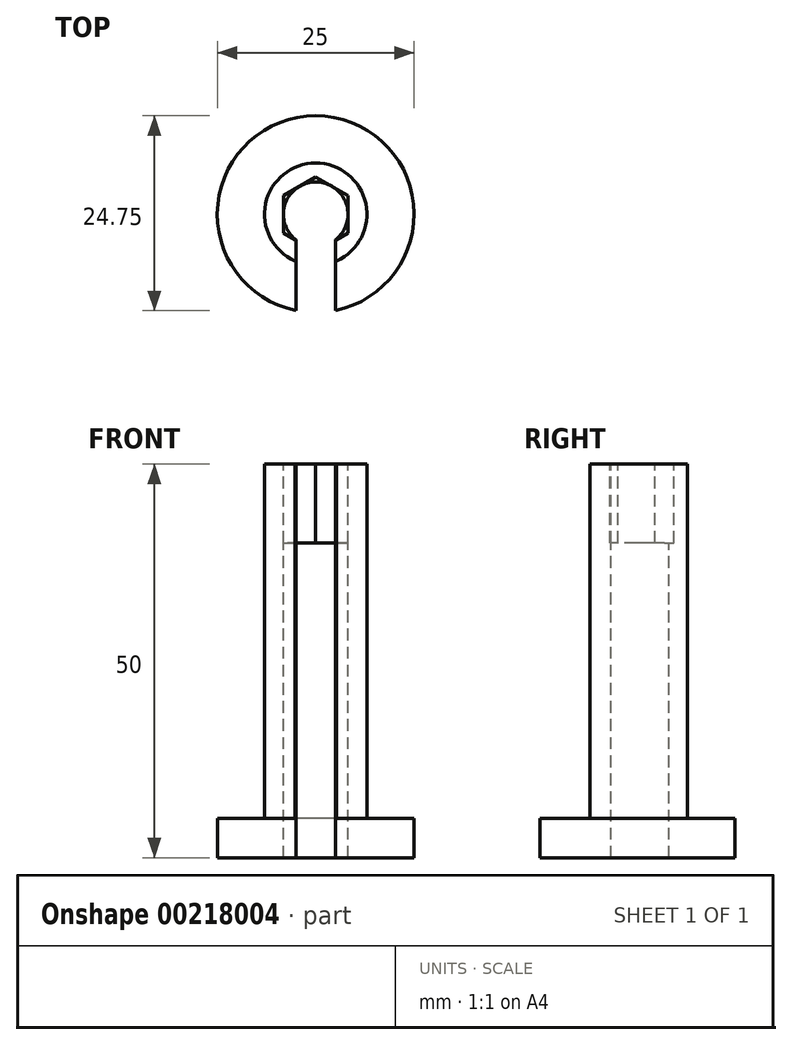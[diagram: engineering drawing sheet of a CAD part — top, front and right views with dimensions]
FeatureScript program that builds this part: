
annotation { "Feature Type Name" : "Feature", "Feature Type Description" : "" }
export const myFeature = defineFeature(function(context is Context, id is Id, definition is map)
    precondition{}
    {
        {
            var Q0;
            Q0=qCreatedBy(makeId("Top.planeOp"),FACE);
            var sketch = newSketch(context, id + "F0", { "sketchPlane" : qUnion([Q0])});
            skCircle(sketch, "E0", {"center": v(0, 0) * mm, "radius": 12.5 * mm});
            skCircle(sketch, "E1", {"center": v(0, 0) * mm, "radius": 6.5 * mm});
            skSolve(sketch);
        }
        {
            var Q0;
            Q0=makeQuery(id+"F0.imprint","IMPRINT",FACE,{"disambiguationData":[TD([[makeQuery(id+"F0.imprint","IMPRINT",EDGE,{"derivedFrom":sQuery(id+"F0.wireOp",EDGE,"E1")}),1.0]])]});
            extrude(context, id + "F1", {"entities" : qUnion([Q0]), "depth" : 50 * mm});
        }
        {
            var Q0;
            Q0 = qSketchRegion(id + "F0", true);
            var Q1;
            Q1 = qSketchRegion(id + "F5", true);
            extrude(context, id + "F2", {"entities" : qUnion([Q0, Q1]), "operationType" : NewBodyOperationType.ADD, "depth" : 5 * mm});
        }
        {
            var Q0;
            Q0=makeQuery(id+"F1.opExtrude","CAP_FACE",FACE,{"disambiguationData":[OSD([sQuery(id+"F0.wireOp",EDGE,"E1")])],"isStart":false});
            var sketch = newSketch(context, id + "F3", { "sketchPlane" : qUnion([Q0])});
            skLineSegment(sketch, "E2", {"start": v(0, 4.73) * mm, "end": v(-4.1, 2.37) * mm});
            skLineSegment(sketch, "E3", {"start": v(-4.1, 2.37) * mm, "end": v(-4.1, -2.37) * mm});
            skLineSegment(sketch, "E4", {"start": v(-4.1, -2.37) * mm, "end": v(0, -4.73) * mm});
            skLineSegment(sketch, "E5", {"start": v(0, -4.73) * mm, "end": v(4.1, -2.37) * mm});
            skLineSegment(sketch, "E6", {"start": v(4.1, -2.37) * mm, "end": v(4.1, 2.37) * mm});
            skLineSegment(sketch, "E7", {"start": v(4.1, 2.37) * mm, "end": v(0, 4.73) * mm});
            skSolve(sketch);
        }
        {
            var Q0;
            Q0=makeQuery(id+"F3.imprint","IMPRINT",FACE,{"disambiguationData":[TD([[makeQuery(id+"F3.imprint","IMPRINT",EDGE,{"derivedFrom":sQuery(id+"F3.wireOp",EDGE,"E2")}),1.0]])]});
            extrude(context, id + "F4", {"entities" : qUnion([Q0]), "operationType" : NewBodyOperationType.REMOVE, "oppositeDirection" : true, "depth" : 10 * mm});
        }
        {
            var Q0;
            Q0=qCreatedBy(makeId("Front.planeOp"),FACE);
            var sketch = newSketch(context, id + "F5", { "sketchPlane" : qUnion([Q0])});
            skSolve(sketch);
        }
        {
            var Q0;
            Q0=makeQuery(id+"F1.opExtrude","CAP_FACE",FACE,{"disambiguationData":[OSD([sQuery(id+"F0.wireOp",EDGE,"E1")])],"isStart":false});
            var sketch = newSketch(context, id + "F6", { "sketchPlane" : qUnion([Q0])});
            skLineSegment(sketch, "E8", {"start": v(-2.5, -3.05) * mm, "end": v(-2.5, -18.05) * mm});
            skLineSegment(sketch, "E9", {"start": v(-2.5, -18.05) * mm, "end": v(2.5, -18.05) * mm});
            skLineSegment(sketch, "E10", {"start": v(2.5, -3.05) * mm, "end": v(-2.5, -3.05) * mm});
            skLineSegment(sketch, "E11", {"start": v(2.5, -3.05) * mm, "end": v(2.5, -18.05) * mm});
            skSolve(sketch);
        }
        {
            var Q0;
            {var subQ7=sQuery(id+"F6.wireOp",EDGE,"E10");Q0=makeQuery(id+"F6.imprint","IMPRINT",FACE,{"disambiguationData":[TD([[makeQuery(id+"F6.imprint","IMPRINT",EDGE,{"derivedFrom":subQ7}),1.0]])]});}
            var Q1;
            {var subQ0=sQuery(id+"F6.wireOp",EDGE,"E8");var subQ1=sQuery(id+"F0.wireOp",EDGE,"E1");var subQ2=makeQuery(id+"F1.opExtrude","CAP_FACE",FACE,{"disambiguationData":[OSD([subQ1])],"isStart":false});var subQ3=makeQuery(id+"Ftp1WgxCQ9i0GfG_1.opChamfer","BLEND_EDGE",EDGE,{"blendedFrom":[makeQuery(id+"F1.opExtrude","CAP_EDGE",EDGE,{"disambiguationData":[OSD([subQ1])],"isStart":false}),subQ2],"blendedInto":[subQ2]});var subQ4=makeQuery(id+"F6.imprint","INTERSECT",VERTEX,{"derivedFrom":[subQ3,subQ0]});Q1=makeQuery(id+"F6.imprint","IMPRINT",FACE,{"disambiguationData":[TD([[makeQuery(id+"F6.imprint","IMPRINT",EDGE,{"disambiguationData":[TD([[subQ4,1.0]])],"derivedFrom":subQ0}),1.0]])]});}
            var Q2;
            {var subQ0=sQuery(id+"F6.wireOp",EDGE,"E9");Q2=makeQuery(id+"F6.imprint","IMPRINT",FACE,{"disambiguationData":[TD([[makeQuery(id+"F6.imprint","IMPRINT",EDGE,{"derivedFrom":subQ0}),1.0]])]});}
            var Q3;
            {var subQ3=sQuery(id+"F6.wireOp",EDGE,"E8");var subQ5=makeQuery(id+"F1.opExtrude","CAP_EDGE",EDGE,{"disambiguationData":[OSD([sQuery(id+"F0.wireOp",EDGE,"E1")])],"isStart":false});var subQ6=makeQuery(id+"F6.imprint","INTERSECT",VERTEX,{"derivedFrom":[subQ5,subQ3]});Q3=makeQuery(id+"F6.imprint","IMPRINT",FACE,{"disambiguationData":[TD([[makeQuery(id+"F6.imprint","IMPRINT",EDGE,{"disambiguationData":[TD([[subQ6,1.0]])],"derivedFrom":subQ3}),1.0]])]});}
            extrude(context, id + "F7", {"entities" : qUnion([Q0, Q1, Q2, Q3]), "operationType" : NewBodyOperationType.REMOVE, "oppositeDirection" : true, "depth" : 55 * mm});
        }
        {
            var Q0;
            Q0=makeQuery(id+"F7.boolean.opBoolean","INTERSECT",EDGE,{"derivedFrom":[makeQuery(id+"F1.opExtrude","SWEPT_FACE",FACE,{"disambiguationData":[OSD([sQuery(id+"F0.wireOp",EDGE,"E1")])]}),makeQuery(id+"F7.opExtrude","SWEPT_FACE",FACE,{"disambiguationData":[OSD([sQuery(id+"F6.wireOp",EDGE,"E8")])]})]});
            var Q1;
            {var subQ0=sQuery(id+"F0.wireOp",EDGE,"E1");Q1=makeQuery(id+"F7.boolean.opBoolean","INTERSECT",EDGE,{"derivedFrom":[makeQuery(id+"Ftp1WgxCQ9i0GfG_1.opChamfer","BLEND_FACE",FACE,{"disambiguationData":[OSD([subQ0]),TDD([makeQuery(id+"F1.opExtrude","CAP_EDGE",EDGE,{"disambiguationData":[OSD([subQ0])],"isStart":false})])]}),makeQuery(id+"F7.opExtrude","SWEPT_FACE",FACE,{"disambiguationData":[OSD([sQuery(id+"F6.wireOp",EDGE,"E8")])]})]});}
            var Q2;
            Q2=makeQuery(id+"F7.boolean.opBoolean","COPY",EDGE,{"derivedFrom":makeQuery(id+"F7.opExtrude","CAP_EDGE",EDGE,{"disambiguationData":[OSD([sQuery(id+"F6.wireOp",EDGE,"E8")])],"isStart":true})});
            var Q3;
            Q3=makeQuery(id+"F7.boolean.opBoolean","INTERSECT",EDGE,{"derivedFrom":[makeQuery(id+"Ftp1WgxCQ9i0GfG_1.opChamfer","BLEND_FACE",FACE,{"disambiguationData":[OSD([sQuery(id+"F3.wireOp",EDGE,"E4")])]}),makeQuery(id+"F7.opExtrude","SWEPT_FACE",FACE,{"disambiguationData":[OSD([sQuery(id+"F6.wireOp",EDGE,"E8")])]})]});
            var Q4;
            {var subQ0=sQuery(id+"F0.wireOp",EDGE,"E1");Q4=makeQuery(id+"F7.boolean.opBoolean","INTERSECT",EDGE,{"derivedFrom":[makeQuery(id+"Ftp1WgxCQ9i0GfG_1.opChamfer","BLEND_FACE",FACE,{"disambiguationData":[OSD([subQ0]),TDD([makeQuery(id+"F1.opExtrude","CAP_EDGE",EDGE,{"disambiguationData":[OSD([subQ0])],"isStart":false})])]}),makeQuery(id+"F7.opExtrude","SWEPT_FACE",FACE,{"disambiguationData":[OSD([sQuery(id+"F6.wireOp",EDGE,"E11")])]})]});}
            var Q5;
            Q5=makeQuery(id+"F7.boolean.opBoolean","COPY",EDGE,{"derivedFrom":makeQuery(id+"F7.opExtrude","CAP_EDGE",EDGE,{"disambiguationData":[OSD([sQuery(id+"F6.wireOp",EDGE,"E11")])],"isStart":true})});
            var Q6;
            Q6=makeQuery(id+"F7.boolean.opBoolean","INTERSECT",EDGE,{"derivedFrom":[makeQuery(id+"F1.opExtrude","SWEPT_FACE",FACE,{"disambiguationData":[OSD([sQuery(id+"F0.wireOp",EDGE,"E1")])]}),makeQuery(id+"F7.opExtrude","SWEPT_FACE",FACE,{"disambiguationData":[OSD([sQuery(id+"F6.wireOp",EDGE,"E11")])]})]});
            var Q7;
            Q7=makeQuery(id+"F7.boolean.opBoolean","INTERSECT",EDGE,{"derivedFrom":[makeQuery(id+"F4.boolean.opBoolean","COPY",FACE,{"derivedFrom":makeQuery(id+"F4.opExtrude","SWEPT_FACE",FACE,{"disambiguationData":[OSD([sQuery(id+"F3.wireOp",EDGE,"E5")])]})}),makeQuery(id+"F7.opExtrude","SWEPT_FACE",FACE,{"disambiguationData":[OSD([sQuery(id+"F6.wireOp",EDGE,"E11")])]})]});
            var Q8;
            Q8=makeQuery(id+"F7.boolean.opBoolean","INTERSECT",EDGE,{"derivedFrom":[makeQuery(id+"Ftp1WgxCQ9i0GfG_1.opChamfer","BLEND_FACE",FACE,{"disambiguationData":[OSD([sQuery(id+"F3.wireOp",EDGE,"E5")])]}),makeQuery(id+"F7.opExtrude","SWEPT_FACE",FACE,{"disambiguationData":[OSD([sQuery(id+"F6.wireOp",EDGE,"E11")])]})]});
            var Q9;
            Q9=makeQuery(id+"F7.boolean.opBoolean","INTERSECT",EDGE,{"derivedFrom":[makeQuery(id+"F4.boolean.opBoolean","COPY",FACE,{"derivedFrom":makeQuery(id+"F4.opExtrude","SWEPT_FACE",FACE,{"disambiguationData":[OSD([sQuery(id+"F3.wireOp",EDGE,"E4")])]})}),makeQuery(id+"F7.opExtrude","SWEPT_FACE",FACE,{"disambiguationData":[OSD([sQuery(id+"F6.wireOp",EDGE,"E8")])]})]});
            var Q10;
            Q10=makeQuery(id+"F7.boolean.opBoolean","INTERSECT",EDGE,{"derivedFrom":[makeQuery(id+"F1.opExtrude","SWEPT_FACE",FACE,{"disambiguationData":[OSD([sQuery(id+"F0.wireOp",EDGE,"E1")])]}),makeQuery(id+"F7.opExtrude","CAP_FACE",FACE,{"disambiguationData":[OSD([sQuery(id+"F6.wireOp",EDGE,"E8"),sQuery(id+"F6.wireOp",EDGE,"E9"),sQuery(id+"F6.wireOp",EDGE,"E10"),sQuery(id+"F6.wireOp",EDGE,"E11")])],"isStart":false})]});
            var Q11;
            Q11=makeQuery(id+"F7.boolean.opBoolean","INTERSECT",EDGE,{"derivedFrom":[makeQuery(id+"F4.boolean.opBoolean","COPY",FACE,{"derivedFrom":makeQuery(id+"F4.opExtrude","SWEPT_FACE",FACE,{"disambiguationData":[OSD([sQuery(id+"F3.wireOp",EDGE,"E4")])]})}),makeQuery(id+"F7.opExtrude","CAP_FACE",FACE,{"disambiguationData":[OSD([sQuery(id+"F6.wireOp",EDGE,"E8"),sQuery(id+"F6.wireOp",EDGE,"E9"),sQuery(id+"F6.wireOp",EDGE,"E10"),sQuery(id+"F6.wireOp",EDGE,"E11")])],"isStart":false})]});
            var Q12;
            Q12=makeQuery(id+"F7.boolean.opBoolean","COPY",EDGE,{"derivedFrom":makeQuery(id+"F7.opExtrude","CAP_EDGE",EDGE,{"disambiguationData":[OSD([sQuery(id+"F6.wireOp",EDGE,"E8")])],"isStart":false})});
            var Q13;
            Q13=makeQuery(id+"F7.boolean.opBoolean","COPY",EDGE,{"derivedFrom":makeQuery(id+"F7.opExtrude","CAP_EDGE",EDGE,{"disambiguationData":[OSD([sQuery(id+"F6.wireOp",EDGE,"E11")])],"isStart":false})});
            var Q14;
            Q14=makeQuery(id+"F7.boolean.opBoolean","INTERSECT",EDGE,{"derivedFrom":[makeQuery(id+"F4.boolean.opBoolean","COPY",FACE,{"derivedFrom":makeQuery(id+"F4.opExtrude","SWEPT_FACE",FACE,{"disambiguationData":[OSD([sQuery(id+"F3.wireOp",EDGE,"E5")])]})}),makeQuery(id+"F7.opExtrude","CAP_FACE",FACE,{"disambiguationData":[OSD([sQuery(id+"F6.wireOp",EDGE,"E8"),sQuery(id+"F6.wireOp",EDGE,"E9"),sQuery(id+"F6.wireOp",EDGE,"E10"),sQuery(id+"F6.wireOp",EDGE,"E11")])],"isStart":false})]});
            chamfer(context, id + "F8", {"entities" : qUnion([Q0, Q1, Q2, Q3, Q4, Q5, Q6, Q7, Q8, Q9, Q10, Q11, Q12, Q13, Q14]), "width" : .1 * mm, "tangentPropagation" : true});
        }
        {
            var Q0;
            Q0=makeQuery(id+"F4.boolean.opBoolean","COPY",FACE,{"derivedFrom":makeQuery(id+"F4.opExtrude","CAP_FACE",FACE,{"disambiguationData":[OSD([sQuery(id+"F3.wireOp",EDGE,"E2"),sQuery(id+"F3.wireOp",EDGE,"E3"),sQuery(id+"F3.wireOp",EDGE,"E4"),sQuery(id+"F3.wireOp",EDGE,"E5"),sQuery(id+"F3.wireOp",EDGE,"E6"),sQuery(id+"F3.wireOp",EDGE,"E7")])],"isStart":false})});
            var sketch = newSketch(context, id + "F9", { "sketchPlane" : qUnion([Q0])});
            skCircle(sketch, "E12", {"center": v(0, 0) * mm, "radius": 4.1 * mm});
            skSolve(sketch);
        }
        {
            var Q0;
            {var subQ1=makeQuery(id+"F4.boolean.opBoolean","COPY",FACE,{"derivedFrom":makeQuery(id+"F4.opExtrude","CAP_FACE",FACE,{"disambiguationData":[OSD([sQuery(id+"F3.wireOp",EDGE,"E2"),sQuery(id+"F3.wireOp",EDGE,"E3"),sQuery(id+"F3.wireOp",EDGE,"E4"),sQuery(id+"F3.wireOp",EDGE,"E5"),sQuery(id+"F3.wireOp",EDGE,"E6"),sQuery(id+"F3.wireOp",EDGE,"E7")])],"isStart":false})});var subQ6=makeQuery(id+"F7.boolean.opBoolean","INTERSECT",EDGE,{"derivedFrom":[subQ1,makeQuery(id+"F7.opExtrude","SWEPT_FACE",FACE,{"disambiguationData":[OSD([sQuery(id+"F6.wireOp",EDGE,"E10")])]})]});Q0=makeQuery(id+"F9.imprint","IMPRINT",FACE,{"disambiguationData":[TD([[makeQuery(id+"F9.imprint","IMPRINT",EDGE,{"derivedFrom":subQ6}),1.0]])]});}
            var Q1;
            {var subQ0=sQuery(id+"F9.wireOp",EDGE,"E12");var subQ3=sQuery(id+"F3.wireOp",EDGE,"E7");var subQ10=makeQuery(id+"F9.imprint","INTERSECT",VERTEX,{"derivedFrom":[makeQuery(id+"F4.boolean.opBoolean","COPY",EDGE,{"derivedFrom":makeQuery(id+"F4.opExtrude","CAP_EDGE",EDGE,{"disambiguationData":[OSD([subQ3])],"isStart":false})}),subQ0]});Q1=makeQuery(id+"F9.imprint","IMPRINT",FACE,{"disambiguationData":[TD([[makeQuery(id+"F9.imprint","IMPRINT",EDGE,{"disambiguationData":[TD([[subQ10,1.0]])],"derivedFrom":subQ0}),1.0]])]});}
            extrude(context, id + "F10", {"entities" : qUnion([Q0, Q1]), "operationType" : NewBodyOperationType.REMOVE, "oppositeDirection" : true, "depth" : 50 * mm});
        }
    });
